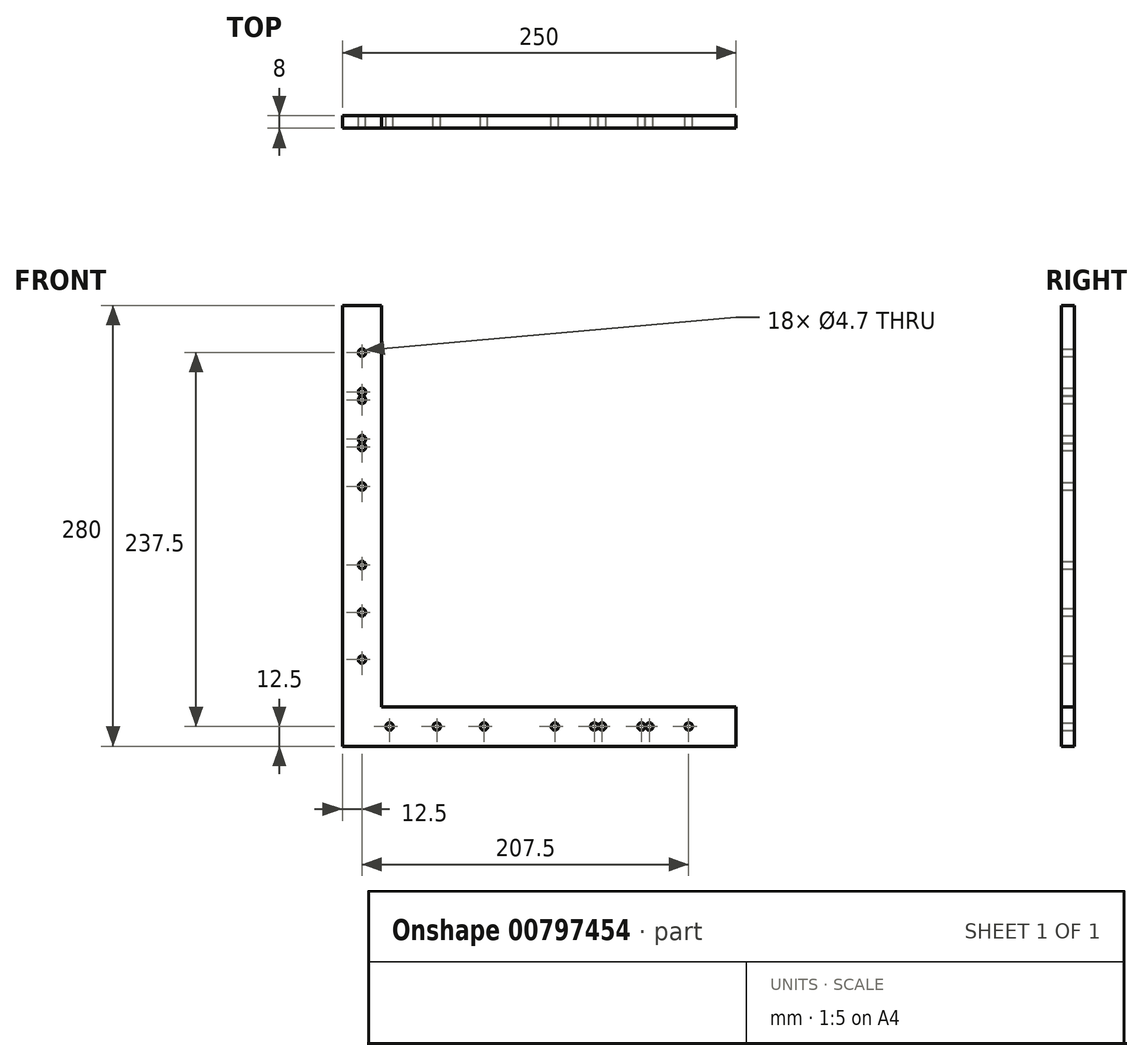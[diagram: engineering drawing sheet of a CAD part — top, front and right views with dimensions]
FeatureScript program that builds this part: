
annotation { "Feature Type Name" : "Feature", "Feature Type Description" : "" }
export const myFeature = defineFeature(function(context is Context, id is Id, definition is map)
    precondition{}
    {
        {
            var Q0;
            Q0=qCreatedBy(makeId("Front.planeOp"),FACE);
            var sketch = newSketch(context, id + "F0", { "sketchPlane" : qUnion([Q0])});
            skLineSegment(sketch, "E0.top", {"start": v(-125, -145) * mm, "end": v(125, -145) * mm});
            skLineSegment(sketch, "E0.left", {"start": v(-125, 135) * mm, "end": v(-125, -145) * mm});
            skLineSegment(sketch, "E0.right", {"start": v(125, -120) * mm, "end": v(125, -145) * mm});
            skPoint(sketch, "E0.middle", {"position": v(0, 0) * mm});
            skLineSegment(sketch, "E1.2", {"start": v(-100, 135) * mm, "end": v(-100, -120) * mm});
            skLineSegment(sketch, "E1.3", {"start": v(-100, -120) * mm, "end": v(125, -120) * mm});
            skLineSegment(sketch, "E2", {"start": v(-100, 135) * mm, "end": v(-125, 135) * mm});
            skLineSegment(sketch, "E3", {"start": v(125, -132.5) * mm, "end": v(289.8, -132.5) * mm, "construction": true});
            skCircle(sketch, "E4", {"center": v(95, -132.5) * mm, "radius": 2.35 * mm});
            skCircle(sketch, "E5", {"center": v(-112.5, 80) * mm, "radius": 2.35 * mm});
            skPoint(sketch, "E5.centerSnap0", {"position": v(-112.5, 135) * mm});
            skCircle(sketch, "E6.0.1.0", {"center": v(-112.5, 50) * mm, "radius": 2.35 * mm});
            skCircle(sketch, "E6.0.2.0", {"center": v(-112.5, 20) * mm, "radius": 2.35 * mm});
            skLineSegment(sketch, "E6.direction1", {"start": v(-112.5, 80) * mm, "end": v(-87.5, 80) * mm, "construction": true});
            skLineSegment(sketch, "E6.direction2", {"start": v(-112.5, 80) * mm, "end": v(-112.5, 50) * mm, "construction": true});
            skCircle(sketch, "E7.1.0.0", {"center": v(65, -132.5) * mm, "radius": 2.35 * mm});
            skCircle(sketch, "E7.2.0.0", {"center": v(35, -132.5) * mm, "radius": 2.35 * mm});
            skLineSegment(sketch, "E7.direction1", {"start": v(95, -132.5) * mm, "end": v(65, -132.5) * mm, "construction": true});
            skCircle(sketch, "E8", {"center": v(70, -132.5) * mm, "radius": 2.35 * mm});
            skCircle(sketch, "E9.1.0.0", {"center": v(40, -132.5) * mm, "radius": 2.35 * mm});
            skCircle(sketch, "E9.2.0.0", {"center": v(10, -132.5) * mm, "radius": 2.35 * mm});
            skLineSegment(sketch, "E9.direction1", {"start": v(70, -132.5) * mm, "end": v(40, -132.5) * mm, "construction": true});
            skCircle(sketch, "E10", {"center": v(-112.5, 105) * mm, "radius": 2.35 * mm});
            skCircle(sketch, "E11.0.1.0", {"center": v(-112.5, 75) * mm, "radius": 2.35 * mm});
            skCircle(sketch, "E11.0.2.0", {"center": v(-112.5, 45) * mm, "radius": 2.35 * mm});
            skLineSegment(sketch, "E11.direction1", {"start": v(-112.5, 105) * mm, "end": v(-87.5, 105) * mm, "construction": true});
            skLineSegment(sketch, "E11.direction2", {"start": v(-112.5, 105) * mm, "end": v(-112.5, 75) * mm, "construction": true});
            skCircle(sketch, "E12", {"center": v(-112.5, -90) * mm, "radius": 2.35 * mm});
            skCircle(sketch, "E13.0.1.0", {"center": v(-112.5, -60) * mm, "radius": 2.35 * mm});
            skCircle(sketch, "E13.0.2.0", {"center": v(-112.5, -30) * mm, "radius": 2.35 * mm});
            skLineSegment(sketch, "E13.direction1", {"start": v(-112.5, -90) * mm, "end": v(-87.5, -90) * mm, "construction": true});
            skLineSegment(sketch, "E13.direction2", {"start": v(-112.5, -90) * mm, "end": v(-112.5, -60) * mm, "construction": true});
            skCircle(sketch, "E14", {"center": v(-95, -132.5) * mm, "radius": 2.35 * mm});
            skCircle(sketch, "E15.1.0.0", {"center": v(-65, -132.5) * mm, "radius": 2.35 * mm});
            skCircle(sketch, "E15.2.0.0", {"center": v(-35, -132.5) * mm, "radius": 2.35 * mm});
            skLineSegment(sketch, "E15.direction1", {"start": v(-95, -132.5) * mm, "end": v(-65, -132.5) * mm, "construction": true});
            skSolve(sketch);
        }
        {
            var Q0;
            Q0 = qSketchRegion(id + "F0", true);
            extrude(context, id + "F1", {"entities" : qUnion([Q0]), "depth" : 8 * mm, "offsetDistance" : 25 * mm});
        }
    });
